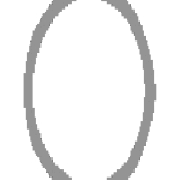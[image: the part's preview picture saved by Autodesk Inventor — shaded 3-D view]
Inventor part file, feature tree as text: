
AUTODESK INVENTOR PART (.ipt)
format: ipt  version: 2021 (Build 250183000, 183)  size: 110,080 bytes
history: native  units: in
note: dims shown in document units (in); Inventor stores cm internally (conversion verified against a paired STEP export)
features: other x4, sketch x3, plane x1
ambient origin geometry x8: Origin, YZ Plane, XZ Plane, XY Plane, X Axis, Y Axis, Z Axis, Center Point
bodies: Solid1 (feature_tree), Body (feature_tree)
feature tree (8):
  other  "Driven Length"
  other  "Frame Generator"
  other  "Start Plane"
  other  "End Plane"
  sketch  "Sketch"  dims[d2=13.5957in d4=-0.0in d5=13.5957in d6=0.12in d7=0.0in d8=90.0deg d9=13.5957in]
  sketch  "Sketch2"  dims[d0=1.0in]
  plane  "Work Plane3"
  sketch  "Sketch3"  dims[d1=0.065in]
